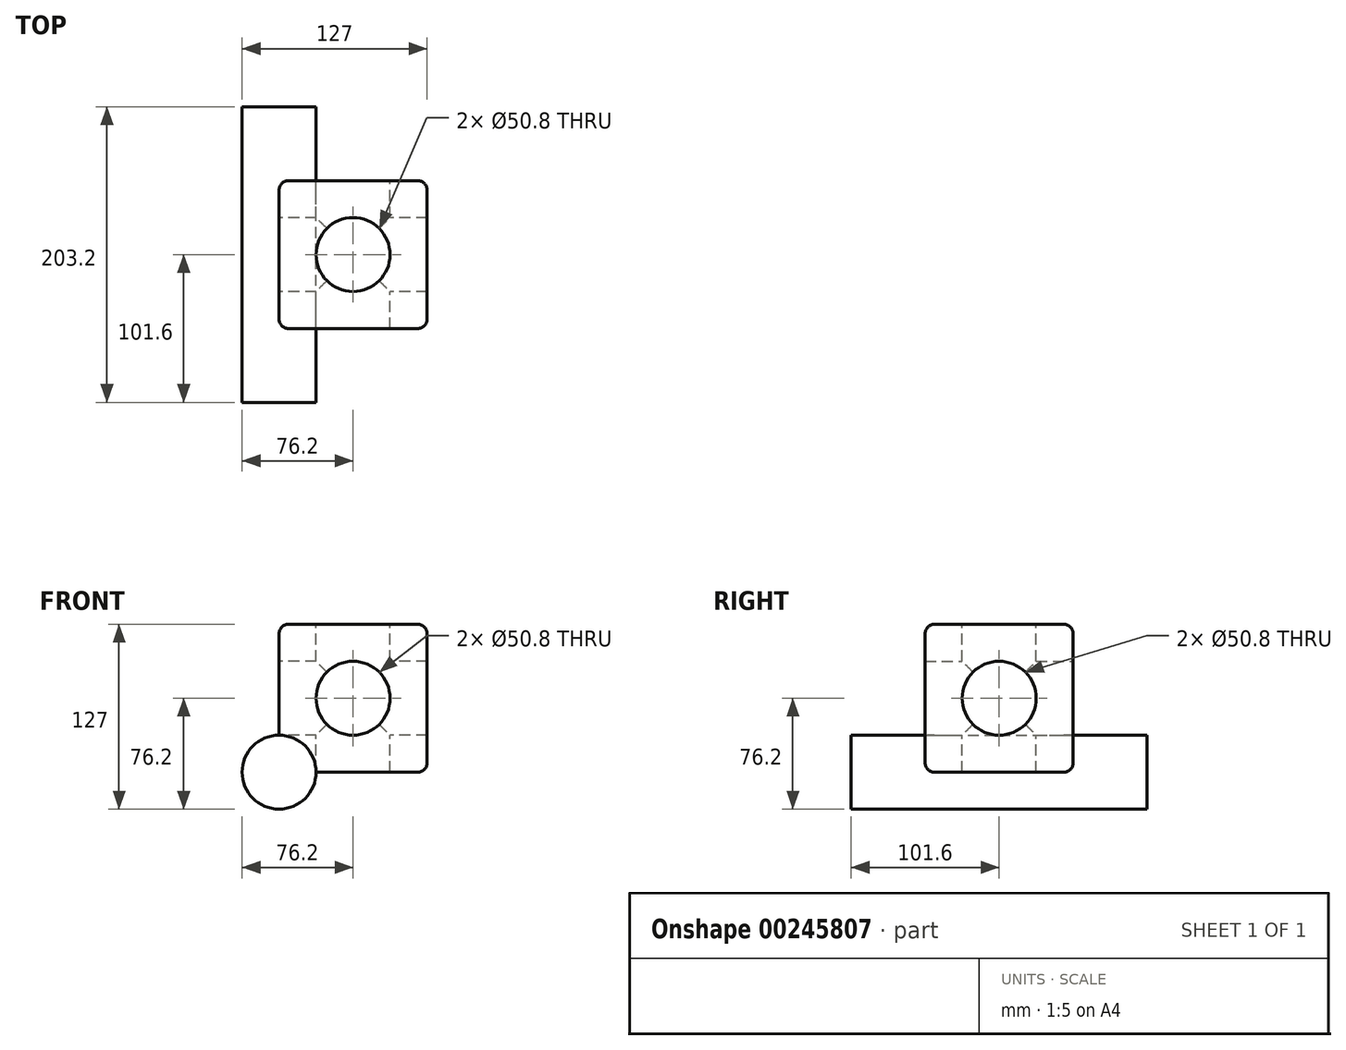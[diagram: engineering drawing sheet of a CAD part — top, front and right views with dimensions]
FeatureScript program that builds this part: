
annotation { "Feature Type Name" : "Feature", "Feature Type Description" : "" }
export const myFeature = defineFeature(function(context is Context, id is Id, definition is map)
    precondition{}
    {
        {
            var Q0;
            Q0=qCreatedBy(makeId("Front.planeOp"),FACE);
            var sketch = newSketch(context, id + "F0", { "sketchPlane" : qUnion([Q0])});
            skLineSegment(sketch, "E0", {"start": v(0, 0) * mm, "end": v(101.6, 0) * mm});
            skLineSegment(sketch, "E1", {"start": v(101.6, 0) * mm, "end": v(101.6, 101.6) * mm});
            skLineSegment(sketch, "E2", {"start": v(101.6, 101.6) * mm, "end": v(0, 101.6) * mm});
            skLineSegment(sketch, "E3", {"start": v(0, 101.6) * mm, "end": v(0, 0) * mm});
            skSolve(sketch);
        }
        {
            var Q0;
            Q0=makeQuery(id+"F0.imprint","IMPRINT",FACE,{"disambiguationData":[TD([[makeQuery(id+"F0.imprint","IMPRINT",EDGE,{"derivedFrom":sQuery(id+"F0.wireOp",EDGE,"E0")}),1.0]])]});
            extrude(context, id + "F1", {"entities" : qUnion([Q0]), "depth" : 101.6 * mm});
        }
        {
            var Q0;
            Q0=makeQuery(id+"F1.opExtrude","SWEPT_FACE",FACE,{"disambiguationData":[OSD([sQuery(id+"F0.wireOp",EDGE,"E2")])]});
            var sketch = newSketch(context, id + "F2", { "sketchPlane" : qUnion([Q0])});
            skCircle(sketch, "E4", {"center": v(50.8, -50.8) * mm, "radius": 25.4 * mm});
            skPoint(sketch, "E5.orphan", {"position": v(50.8, 0) * mm});
            skPoint(sketch, "E6.end.orphan", {"position": v(50.8, -101.6) * mm});
            skSolve(sketch);
        }
        {
            var Q0;
            Q0 = qSketchRegion(id + "F2", true);
            extrude(context, id + "F3", {"entities" : qUnion([Q0]), "operationType" : NewBodyOperationType.REMOVE, "oppositeDirection" : true, "depth" : 101.6 * mm});
        }
        {
            var Q0;
            Q0=makeQuery(id+"F1.opExtrude","CAP_FACE",FACE,{"disambiguationData":[OSD([sQuery(id+"F0.wireOp",EDGE,"E0"),sQuery(id+"F0.wireOp",EDGE,"E1"),sQuery(id+"F0.wireOp",EDGE,"E2"),sQuery(id+"F0.wireOp",EDGE,"E3")])],"isStart":true});
            var sketch = newSketch(context, id + "F4", { "sketchPlane" : qUnion([Q0])});
            skCircle(sketch, "E7", {"center": v(-50.8, 50.8) * mm, "radius": 25.4 * mm});
            skPoint(sketch, "E8.orphan", {"position": v(-50.8, 101.6) * mm});
            skPoint(sketch, "E9.end.orphan", {"position": v(-50.8, 0) * mm});
            skSolve(sketch);
        }
        {
            var Q0;
            Q0 = qSketchRegion(id + "F4", true);
            extrude(context, id + "F5", {"entities" : qUnion([Q0]), "operationType" : NewBodyOperationType.REMOVE, "oppositeDirection" : true, "depth" : 101.6 * mm});
        }
        {
            var Q0;
            Q0=makeQuery(id+"F1.opExtrude","SWEPT_FACE",FACE,{"disambiguationData":[OSD([sQuery(id+"F0.wireOp",EDGE,"E3")])]});
            var sketch = newSketch(context, id + "F6", { "sketchPlane" : qUnion([Q0])});
            skCircle(sketch, "E10", {"center": v(50.8, 50.8) * mm, "radius": 25.4 * mm});
            skPoint(sketch, "E11.orphan", {"position": v(50.8, 101.6) * mm});
            skPoint(sketch, "E12.end.orphan", {"position": v(50.8, 0) * mm});
            skSolve(sketch);
        }
        {
            var Q0;
            Q0 = qSketchRegion(id + "F6", true);
            extrude(context, id + "F7", {"entities" : qUnion([Q0]), "operationType" : NewBodyOperationType.REMOVE, "oppositeDirection" : true, "depth" : 101.6 * mm});
        }
        {
            var Q0;
            Q0=makeQuery(id+"F1.opExtrude","SWEPT_EDGE",EDGE,{"disambiguationData":[OSD([sQuery(id+"F0.wireOp",EDGE,"E2"),sQuery(id+"F0.wireOp",EDGE,"E3")])]});
            var Q1;
            Q1=makeQuery(id+"F1.opExtrude","CAP_EDGE",EDGE,{"disambiguationData":[OSD([sQuery(id+"F0.wireOp",EDGE,"E2")])],"isStart":true});
            var Q2;
            Q2=makeQuery(id+"F1.opExtrude","SWEPT_EDGE",EDGE,{"disambiguationData":[OSD([sQuery(id+"F0.wireOp",EDGE,"E1"),sQuery(id+"F0.wireOp",EDGE,"E2")])]});
            var Q3;
            Q3=makeQuery(id+"F1.opExtrude","CAP_EDGE",EDGE,{"disambiguationData":[OSD([sQuery(id+"F0.wireOp",EDGE,"E2")])],"isStart":false});
            var Q4;
            Q4=makeQuery(id+"F1.opExtrude","CAP_EDGE",EDGE,{"disambiguationData":[OSD([sQuery(id+"F0.wireOp",EDGE,"E1")])],"isStart":false});
            var Q5;
            Q5=makeQuery(id+"F1.opExtrude","CAP_EDGE",EDGE,{"disambiguationData":[OSD([sQuery(id+"F0.wireOp",EDGE,"E3")])],"isStart":false});
            var Q6;
            Q6=makeQuery(id+"F1.opExtrude","CAP_EDGE",EDGE,{"disambiguationData":[OSD([sQuery(id+"F0.wireOp",EDGE,"E0")])],"isStart":false});
            var Q7;
            Q7=makeQuery(id+"F1.opExtrude","CAP_EDGE",EDGE,{"disambiguationData":[OSD([sQuery(id+"F0.wireOp",EDGE,"E1")])],"isStart":true});
            var Q8;
            Q8=makeQuery(id+"F1.opExtrude","SWEPT_EDGE",EDGE,{"disambiguationData":[OSD([sQuery(id+"F0.wireOp",EDGE,"E0"),sQuery(id+"F0.wireOp",EDGE,"E1")])]});
            fillet(context, id + "F8", {"entities" : qUnion([Q0, Q1, Q2, Q3, Q4, Q5, Q6, Q7, Q8]), "radius" : 6.35 * mm, "tangentPropagation" : true, "allowEdgeOverflow" : false});
        }
        {
            var Q0;
            Q0=makeQuery(id+"F1.opExtrude","CAP_EDGE",EDGE,{"disambiguationData":[OSD([sQuery(id+"F0.wireOp",EDGE,"E0")])],"isStart":true});
            var Q1;
            Q1=makeQuery(id+"F1.opExtrude","CAP_EDGE",EDGE,{"disambiguationData":[OSD([sQuery(id+"F0.wireOp",EDGE,"E3")])],"isStart":true});
            fillet(context, id + "F9", {"entities" : qUnion([Q0, Q1]), "radius" : 6.35 * mm, "tangentPropagation" : true, "allowEdgeOverflow" : false});
        }
        {
            var Q0;
            Q0=makeQuery(id+"F1.opExtrude","SWEPT_EDGE",EDGE,{"disambiguationData":[OSD([sQuery(id+"F0.wireOp",EDGE,"E0"),sQuery(id+"F0.wireOp",EDGE,"E3")])]});
            fillet(context, id + "F10", {"entities" : qUnion([Q0]), "radius" : 6.35 * mm, "tangentPropagation" : true, "allowEdgeOverflow" : false});
        }
        {
            var Q0;
            Q0=qCreatedBy(makeId("Front.planeOp"),FACE);
            cPlane(context, id + "F11", {"entities" : qUnion([Q0]), "cplaneType" : CPlaneType.OFFSET, "offset" : 101.6 * mm, "width" : 152.4 * mm, "height" : 152.4 * mm});
        }
        {
            var Q0;
            Q0=qCreatedBy(id+"F11.planeOp",FACE);
            var sketch = newSketch(context, id + "F12", { "sketchPlane" : qUnion([Q0])});
            skCircle(sketch, "E13", {"center": v(0, 0) * mm, "radius": 25.4 * mm});
            skSolve(sketch);
        }
        {
            var Q0;
            Q0 = qSketchRegion(id + "F12", true);
            extrude(context, id + "F13", {"entities" : qUnion([Q0]), "operationType" : NewBodyOperationType.ADD, "depth" : 50.8 * mm, "hasSecondDirection" : true, "secondDirectionOppositeDirection" : true, "secondDirectionDepth" : 152.4 * mm});
        }
    });
